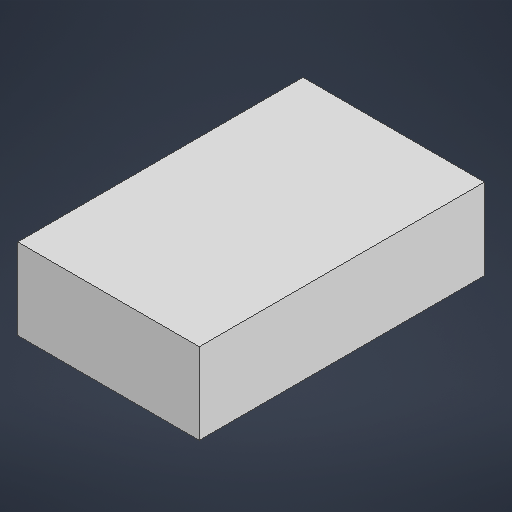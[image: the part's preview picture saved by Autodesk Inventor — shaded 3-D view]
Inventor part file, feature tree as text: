
AUTODESK INVENTOR PART (.ipt)
format: ipt  version: 2025.2 (Build 292293000, 293)  size: 162,816 bytes
history: native  units: mm
features: sketch x3, extrude x2
ambient origin geometry x8: Origin, YZ Plane, XZ Plane, XY Plane, X Axis, Y Axis, Z Axis, Center Point
bodies: Solid1 (feature_tree)
feature tree (5):
  sketch  "Sketch1"  dims[d0=56.0mm d1=88.0mm]
  extrude  "Extrusion1"  Depth=88.0mm
  extrude  "Extrusion2"  Depth=11.0mm
  sketch  "Sketch2"  dims[d2=25.0mm d3=0.0mm d4=11.0mm]
  sketch  "Sketch3"  dims[d5=1.0mm d6=7.0mm d7=3.0mm d8=0.0mm]
